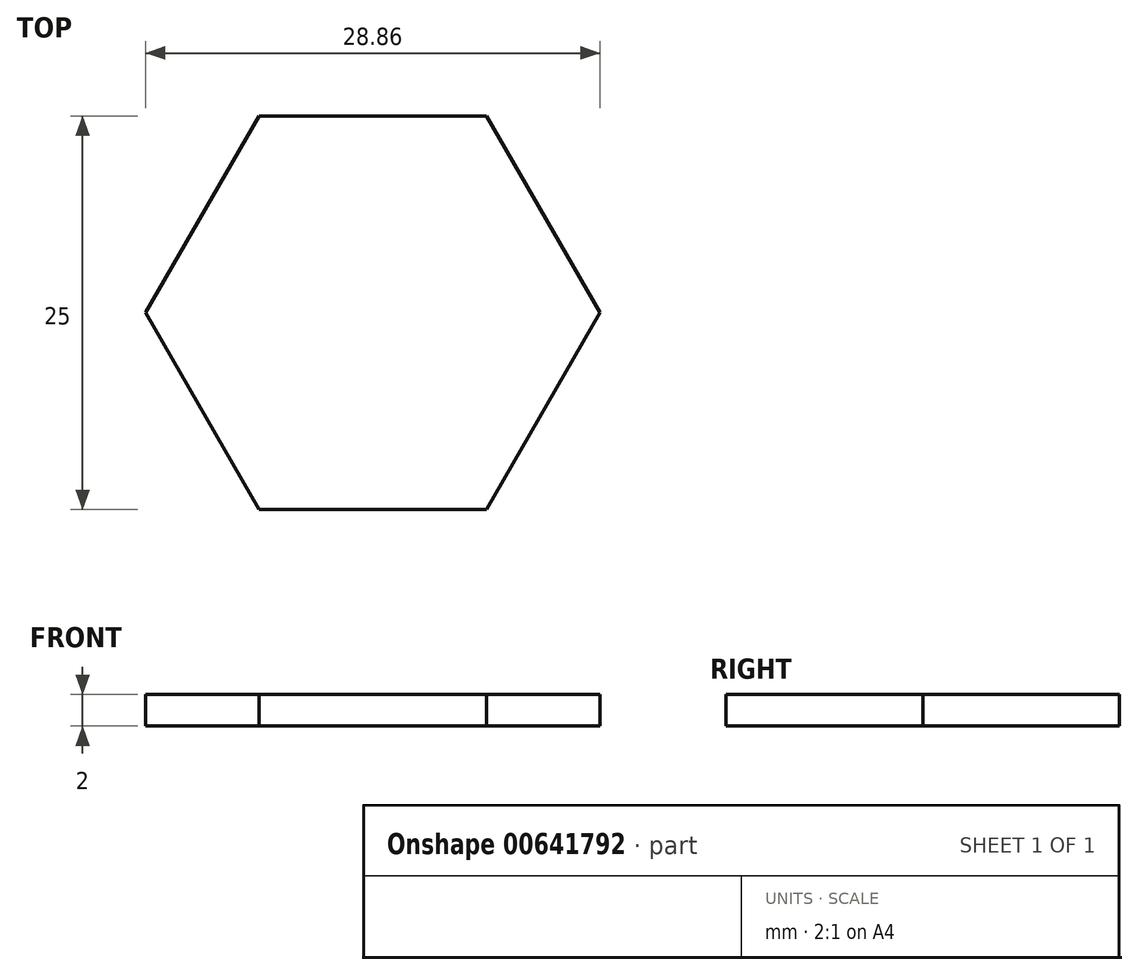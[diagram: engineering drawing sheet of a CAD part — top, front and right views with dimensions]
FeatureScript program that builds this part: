
annotation { "Feature Type Name" : "Feature", "Feature Type Description" : "" }
export const myFeature = defineFeature(function(context is Context, id is Id, definition is map)
    precondition{}
    {
        {
            var Q0;
            Q0=qCreatedBy(makeId("Top.planeOp"),FACE);
            var sketch = newSketch(context, id + "F0", { "sketchPlane" : qUnion([Q0])});
            skCircle(sketch, "E0.cCircle", {"center": v(0, 0) * mm, "radius": 12.5 * mm, "construction": true});
            skLineSegment(sketch, "E0.0", {"start": v(-7.22, 12.5) * mm, "end": v(7.22, 12.5) * mm});
            skLineSegment(sketch, "E0.1", {"start": v(7.22, 12.5) * mm, "end": v(14.43, 0) * mm});
            skLineSegment(sketch, "E0.2", {"start": v(14.43, 0) * mm, "end": v(7.22, -12.5) * mm});
            skLineSegment(sketch, "E0.3", {"start": v(7.22, -12.5) * mm, "end": v(-7.22, -12.5) * mm});
            skLineSegment(sketch, "E0.4", {"start": v(-7.22, -12.5) * mm, "end": v(-14.43, 0) * mm});
            skLineSegment(sketch, "E0.5", {"start": v(-14.43, 0) * mm, "end": v(-7.22, 12.5) * mm});
            skPoint(sketch, "E0.0.midPoint", {"position": v(0, 12.5) * mm});
            skSolve(sketch);
        }
        {
            var Q0;
            Q0=makeQuery(id+"F0.imprint","IMPRINT",FACE,{"disambiguationData":[TD([[makeQuery(id+"F0.imprint","IMPRINT",EDGE,{"derivedFrom":sQuery(id+"F0.wireOp",EDGE,"E0.0")}),-1.0]])]});
            extrude(context, id + "F1", {"entities" : qUnion([Q0]), "depth" : 2 * mm, "offsetDistance" : 25 * mm});
        }
    });
